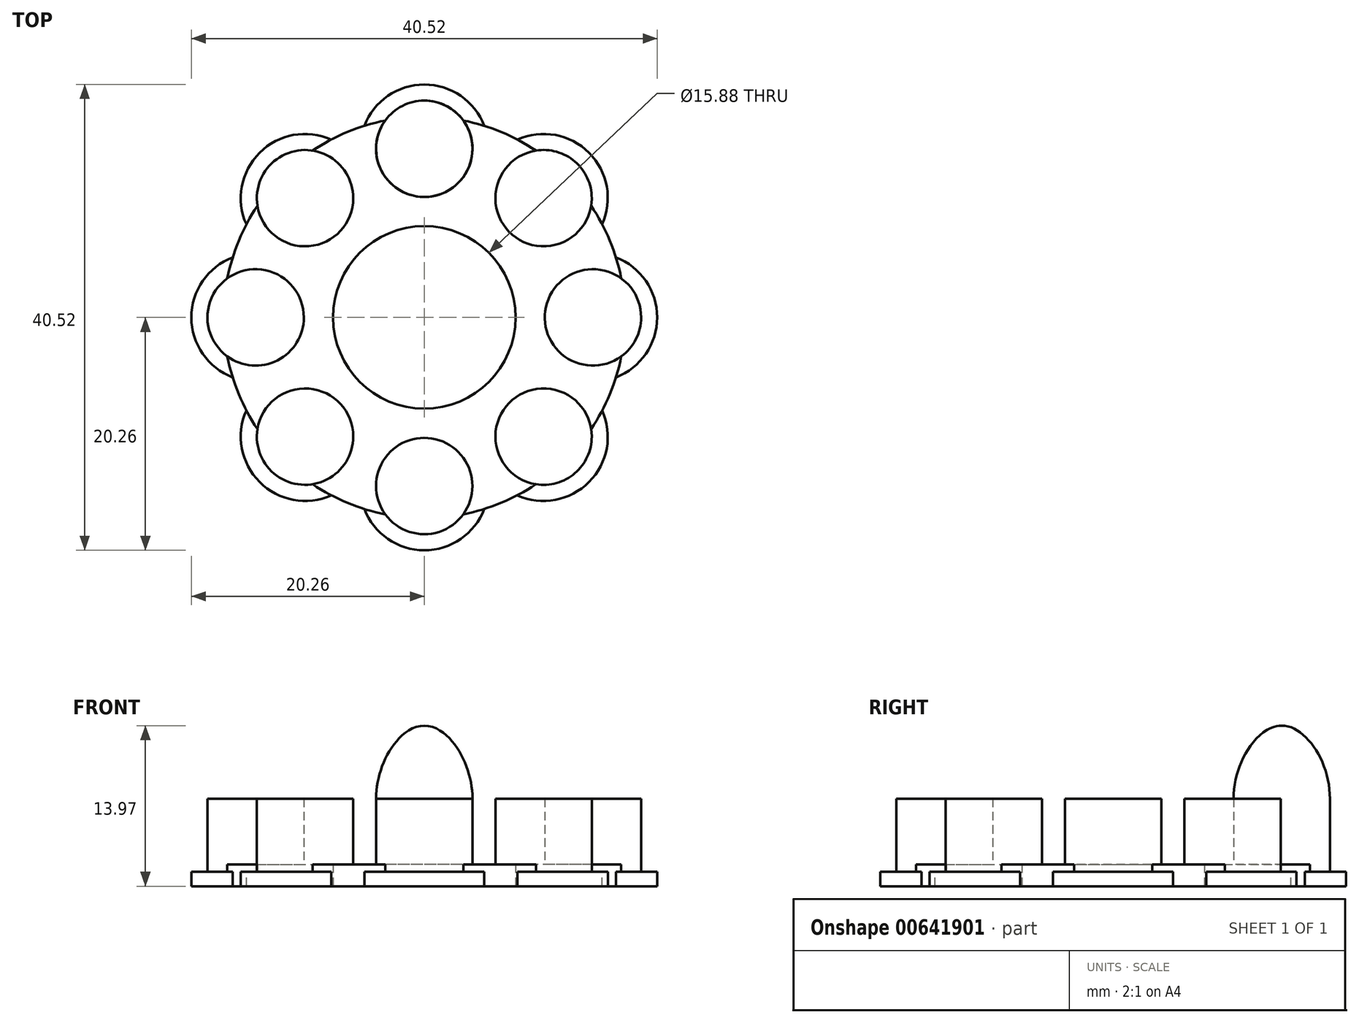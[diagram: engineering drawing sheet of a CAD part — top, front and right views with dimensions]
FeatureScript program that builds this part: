
annotation { "Feature Type Name" : "Feature", "Feature Type Description" : "" }
export const myFeature = defineFeature(function(context is Context, id is Id, definition is map)
    precondition{}
    {
        {
            var Q0;
            Q0=qCreatedBy(makeId("Top.planeOp"),FACE);
            var sketch = newSketch(context, id + "F0", { "sketchPlane" : qUnion([Q0])});
            skCircle(sketch, "E0", {"center": v(0, 14.67) * mm, "radius": 5.59 * mm});
            skCircle(sketch, "E1", {"center": v(0, 0) * mm, "radius": 7.94 * mm});
            skCircle(sketch, "E2", {"center": v(0, 14.67) * mm, "radius": 4.2 * mm});
            skCircle(sketch, "E3", {"center": v(0, 0) * mm, "radius": 17.46 * mm});
            skCircle(sketch, "E4.1.0", {"center": v(-10.37, 10.37) * mm, "radius": 4.2 * mm});
            skCircle(sketch, "E4.1.1", {"center": v(-10.37, 10.37) * mm, "radius": 5.59 * mm});
            skCircle(sketch, "E4.2.0", {"center": v(-14.67, 0) * mm, "radius": 4.2 * mm});
            skCircle(sketch, "E4.2.1", {"center": v(-14.67, 0) * mm, "radius": 5.59 * mm});
            skCircle(sketch, "E5.1.3.0", {"center": v(-10.37, -10.37) * mm, "radius": 4.2 * mm});
            skCircle(sketch, "E5.2.3.0", {"center": v(-10.37, -10.37) * mm, "radius": 5.59 * mm});
            skCircle(sketch, "E5.1.4.0", {"center": v(0, -14.67) * mm, "radius": 4.2 * mm});
            skCircle(sketch, "E5.2.4.0", {"center": v(0, -14.67) * mm, "radius": 5.59 * mm});
            skCircle(sketch, "E5.1.5.0", {"center": v(10.37, -10.37) * mm, "radius": 4.2 * mm});
            skCircle(sketch, "E5.2.5.0", {"center": v(10.37, -10.37) * mm, "radius": 5.59 * mm});
            skCircle(sketch, "E5.1.6.0", {"center": v(14.67, 0) * mm, "radius": 4.2 * mm});
            skCircle(sketch, "E5.2.6.0", {"center": v(14.67, 0) * mm, "radius": 5.59 * mm});
            skCircle(sketch, "E5.1.7.0", {"center": v(10.37, 10.37) * mm, "radius": 4.2 * mm});
            skCircle(sketch, "E5.2.7.0", {"center": v(10.37, 10.37) * mm, "radius": 5.59 * mm});
            skSolve(sketch);
        }
        {
            var Q0;
            {var subQ0=sQuery(id+"F0.wireOp",EDGE,"E3");var subQ1=sQuery(id+"F0.wireOp",EDGE,"E0");var subQ2=makeQuery(id+"F0.imprint","INTERSECT",VERTEX,{"disambiguationData":[OD(0.0)],"derivedFrom":[subQ1,subQ0]});Q0=makeQuery(id+"F0.imprint","IMPRINT",FACE,{"disambiguationData":[TD([[makeQuery(id+"F0.imprint","IMPRINT",EDGE,{"disambiguationData":[TD([[subQ2,1.0]])],"derivedFrom":subQ1}),1.0]])]});}
            var Q1;
            {var subQ0=sQuery(id+"F0.wireOp",EDGE,"E5.2.7.0");var subQ1=sQuery(id+"F0.wireOp",EDGE,"E3");var subQ2=makeQuery(id+"F0.imprint","INTERSECT",VERTEX,{"disambiguationData":[OD(0.0)],"derivedFrom":[subQ1,subQ0]});Q1=makeQuery(id+"F0.imprint","IMPRINT",FACE,{"disambiguationData":[TD([[makeQuery(id+"F0.imprint","IMPRINT",EDGE,{"disambiguationData":[TD([[subQ2,-1.0]])],"derivedFrom":subQ1}),1.0]])]});}
            var Q2;
            {var subQ0=sQuery(id+"F0.wireOp",EDGE,"E5.2.6.0");var subQ1=sQuery(id+"F0.wireOp",EDGE,"E3");var subQ2=makeQuery(id+"F0.imprint","INTERSECT",VERTEX,{"disambiguationData":[OD(0.0)],"derivedFrom":[subQ1,subQ0]});Q2=makeQuery(id+"F0.imprint","IMPRINT",FACE,{"disambiguationData":[TD([[makeQuery(id+"F0.imprint","IMPRINT",EDGE,{"disambiguationData":[TD([[subQ2,1.0]])],"derivedFrom":subQ1}),1.0]])]});}
            var Q3;
            {var subQ0=sQuery(id+"F0.wireOp",EDGE,"E5.2.5.0");var subQ1=sQuery(id+"F0.wireOp",EDGE,"E3");var subQ2=makeQuery(id+"F0.imprint","INTERSECT",VERTEX,{"disambiguationData":[OD(0.0)],"derivedFrom":[subQ1,subQ0]});Q3=makeQuery(id+"F0.imprint","IMPRINT",FACE,{"disambiguationData":[TD([[makeQuery(id+"F0.imprint","IMPRINT",EDGE,{"disambiguationData":[TD([[subQ2,-1.0]])],"derivedFrom":subQ1}),1.0]])]});}
            var Q4;
            {var subQ0=sQuery(id+"F0.wireOp",EDGE,"E5.2.4.0");var subQ1=sQuery(id+"F0.wireOp",EDGE,"E3");var subQ2=makeQuery(id+"F0.imprint","INTERSECT",VERTEX,{"disambiguationData":[OD(0.0)],"derivedFrom":[subQ1,subQ0]});Q4=makeQuery(id+"F0.imprint","IMPRINT",FACE,{"disambiguationData":[TD([[makeQuery(id+"F0.imprint","IMPRINT",EDGE,{"disambiguationData":[TD([[subQ2,-1.0]])],"derivedFrom":subQ1}),1.0]])]});}
            var Q5;
            {var subQ0=sQuery(id+"F0.wireOp",EDGE,"E5.2.3.0");var subQ1=sQuery(id+"F0.wireOp",EDGE,"E3");var subQ2=makeQuery(id+"F0.imprint","INTERSECT",VERTEX,{"disambiguationData":[OD(0.0)],"derivedFrom":[subQ1,subQ0]});Q5=makeQuery(id+"F0.imprint","IMPRINT",FACE,{"disambiguationData":[TD([[makeQuery(id+"F0.imprint","IMPRINT",EDGE,{"disambiguationData":[TD([[subQ2,-1.0]])],"derivedFrom":subQ1}),1.0]])]});}
            var Q6;
            {var subQ0=sQuery(id+"F0.wireOp",EDGE,"E4.2.1");var subQ1=sQuery(id+"F0.wireOp",EDGE,"E3");var subQ2=makeQuery(id+"F0.imprint","INTERSECT",VERTEX,{"disambiguationData":[OD(0.0)],"derivedFrom":[subQ1,subQ0]});Q6=makeQuery(id+"F0.imprint","IMPRINT",FACE,{"disambiguationData":[TD([[makeQuery(id+"F0.imprint","IMPRINT",EDGE,{"disambiguationData":[TD([[subQ2,-1.0]])],"derivedFrom":subQ1}),1.0]])]});}
            var Q7;
            {var subQ0=sQuery(id+"F0.wireOp",EDGE,"E4.1.1");var subQ1=sQuery(id+"F0.wireOp",EDGE,"E3");var subQ2=makeQuery(id+"F0.imprint","INTERSECT",VERTEX,{"disambiguationData":[OD(0.0)],"derivedFrom":[subQ1,subQ0]});Q7=makeQuery(id+"F0.imprint","IMPRINT",FACE,{"disambiguationData":[TD([[makeQuery(id+"F0.imprint","IMPRINT",EDGE,{"disambiguationData":[TD([[subQ2,-1.0]])],"derivedFrom":subQ1}),1.0]])]});}
            var Q8;
            Q8=makeQuery(id+"F0.imprint","IMPRINT",FACE,{"disambiguationData":[TD([[makeQuery(id+"F0.imprint","IMPRINT",EDGE,{"derivedFrom":sQuery(id+"F0.wireOp",EDGE,"E1")}),-1.0]])]});
            extrude(context, id + "F1", {"entities" : qUnion([Q0, Q1, Q2, Q3, Q4, Q5, Q6, Q7, Q8]), "depth" : 0.64 * mm, "offsetDistance" : 25.4 * mm});
        }
        {
            var Q0;
            Q0=qSketchRegion(id+"F0",true);
            var Q1;
            {var subQ0=sQuery(id+"F0.wireOp",EDGE,"E5.1.4.0");var subQ1=sQuery(id+"F0.wireOp",EDGE,"E3");var subQ2=makeQuery(id+"F0.imprint","INTERSECT",VERTEX,{"disambiguationData":[OD(0.0)],"derivedFrom":[subQ1,subQ0]});Q1=makeQuery(id+"F0.imprint","IMPRINT",FACE,{"disambiguationData":[TD([[makeQuery(id+"F0.imprint","IMPRINT",EDGE,{"disambiguationData":[TD([[subQ2,-1.0]])],"derivedFrom":subQ1}),-1.0]])]});}
            var Q2;
            {var subQ0=sQuery(id+"F0.wireOp",EDGE,"E5.1.4.0");var subQ1=sQuery(id+"F0.wireOp",EDGE,"E3");var subQ2=makeQuery(id+"F0.imprint","INTERSECT",VERTEX,{"disambiguationData":[OD(0.0)],"derivedFrom":[subQ1,subQ0]});Q2=makeQuery(id+"F0.imprint","IMPRINT",FACE,{"disambiguationData":[TD([[makeQuery(id+"F0.imprint","IMPRINT",EDGE,{"disambiguationData":[TD([[subQ2,-1.0]])],"derivedFrom":subQ1}),1.0]])]});}
            var Q3;
            {var subQ0=sQuery(id+"F0.wireOp",EDGE,"E5.1.5.0");var subQ1=sQuery(id+"F0.wireOp",EDGE,"E3");var subQ2=makeQuery(id+"F0.imprint","INTERSECT",VERTEX,{"disambiguationData":[OD(0.0)],"derivedFrom":[subQ1,subQ0]});Q3=makeQuery(id+"F0.imprint","IMPRINT",FACE,{"disambiguationData":[TD([[makeQuery(id+"F0.imprint","IMPRINT",EDGE,{"disambiguationData":[TD([[subQ2,-1.0]])],"derivedFrom":subQ1}),1.0]])]});}
            var Q4;
            {var subQ0=sQuery(id+"F0.wireOp",EDGE,"E5.1.5.0");var subQ1=sQuery(id+"F0.wireOp",EDGE,"E3");var subQ2=makeQuery(id+"F0.imprint","INTERSECT",VERTEX,{"disambiguationData":[OD(0.0)],"derivedFrom":[subQ1,subQ0]});Q4=makeQuery(id+"F0.imprint","IMPRINT",FACE,{"disambiguationData":[TD([[makeQuery(id+"F0.imprint","IMPRINT",EDGE,{"disambiguationData":[TD([[subQ2,-1.0]])],"derivedFrom":subQ1}),-1.0]])]});}
            var Q5;
            {var subQ0=sQuery(id+"F0.wireOp",EDGE,"E5.1.6.0");var subQ1=sQuery(id+"F0.wireOp",EDGE,"E3");var subQ2=makeQuery(id+"F0.imprint","INTERSECT",VERTEX,{"disambiguationData":[OD(0.0)],"derivedFrom":[subQ1,subQ0]});Q5=makeQuery(id+"F0.imprint","IMPRINT",FACE,{"disambiguationData":[TD([[makeQuery(id+"F0.imprint","IMPRINT",EDGE,{"disambiguationData":[TD([[subQ2,1.0]])],"derivedFrom":subQ1}),-1.0]])]});}
            var Q6;
            {var subQ0=sQuery(id+"F0.wireOp",EDGE,"E5.1.6.0");var subQ1=sQuery(id+"F0.wireOp",EDGE,"E3");var subQ2=makeQuery(id+"F0.imprint","INTERSECT",VERTEX,{"disambiguationData":[OD(0.0)],"derivedFrom":[subQ1,subQ0]});Q6=makeQuery(id+"F0.imprint","IMPRINT",FACE,{"disambiguationData":[TD([[makeQuery(id+"F0.imprint","IMPRINT",EDGE,{"disambiguationData":[TD([[subQ2,1.0]])],"derivedFrom":subQ1}),1.0]])]});}
            var Q7;
            {var subQ0=sQuery(id+"F0.wireOp",EDGE,"E5.1.7.0");var subQ1=sQuery(id+"F0.wireOp",EDGE,"E3");var subQ2=makeQuery(id+"F0.imprint","INTERSECT",VERTEX,{"disambiguationData":[OD(0.0)],"derivedFrom":[subQ1,subQ0]});Q7=makeQuery(id+"F0.imprint","IMPRINT",FACE,{"disambiguationData":[TD([[makeQuery(id+"F0.imprint","IMPRINT",EDGE,{"disambiguationData":[TD([[subQ2,-1.0]])],"derivedFrom":subQ1}),1.0]])]});}
            var Q8;
            {var subQ0=sQuery(id+"F0.wireOp",EDGE,"E5.1.7.0");var subQ1=sQuery(id+"F0.wireOp",EDGE,"E3");var subQ2=makeQuery(id+"F0.imprint","INTERSECT",VERTEX,{"disambiguationData":[OD(0.0)],"derivedFrom":[subQ1,subQ0]});Q8=makeQuery(id+"F0.imprint","IMPRINT",FACE,{"disambiguationData":[TD([[makeQuery(id+"F0.imprint","IMPRINT",EDGE,{"disambiguationData":[TD([[subQ2,-1.0]])],"derivedFrom":subQ1}),-1.0]])]});}
            var Q9;
            {var subQ0=sQuery(id+"F0.wireOp",EDGE,"E4.1.0");var subQ1=sQuery(id+"F0.wireOp",EDGE,"E3");var subQ2=makeQuery(id+"F0.imprint","INTERSECT",VERTEX,{"disambiguationData":[OD(0.0)],"derivedFrom":[subQ1,subQ0]});Q9=makeQuery(id+"F0.imprint","IMPRINT",FACE,{"disambiguationData":[TD([[makeQuery(id+"F0.imprint","IMPRINT",EDGE,{"disambiguationData":[TD([[subQ2,-1.0]])],"derivedFrom":subQ1}),1.0]])]});}
            var Q10;
            {var subQ0=sQuery(id+"F0.wireOp",EDGE,"E4.1.0");var subQ1=sQuery(id+"F0.wireOp",EDGE,"E3");var subQ2=makeQuery(id+"F0.imprint","INTERSECT",VERTEX,{"disambiguationData":[OD(0.0)],"derivedFrom":[subQ1,subQ0]});Q10=makeQuery(id+"F0.imprint","IMPRINT",FACE,{"disambiguationData":[TD([[makeQuery(id+"F0.imprint","IMPRINT",EDGE,{"disambiguationData":[TD([[subQ2,-1.0]])],"derivedFrom":subQ1}),-1.0]])]});}
            var Q11;
            {var subQ0=sQuery(id+"F0.wireOp",EDGE,"E4.2.0");var subQ1=sQuery(id+"F0.wireOp",EDGE,"E3");var subQ2=makeQuery(id+"F0.imprint","INTERSECT",VERTEX,{"disambiguationData":[OD(0.0)],"derivedFrom":[subQ1,subQ0]});Q11=makeQuery(id+"F0.imprint","IMPRINT",FACE,{"disambiguationData":[TD([[makeQuery(id+"F0.imprint","IMPRINT",EDGE,{"disambiguationData":[TD([[subQ2,-1.0]])],"derivedFrom":subQ1}),1.0]])]});}
            var Q12;
            {var subQ0=sQuery(id+"F0.wireOp",EDGE,"E3");var subQ1=sQuery(id+"F0.wireOp",EDGE,"E2");var subQ2=makeQuery(id+"F0.imprint","INTERSECT",VERTEX,{"disambiguationData":[OD(0.0)],"derivedFrom":[subQ1,subQ0]});Q12=makeQuery(id+"F0.imprint","IMPRINT",FACE,{"disambiguationData":[TD([[makeQuery(id+"F0.imprint","IMPRINT",EDGE,{"disambiguationData":[TD([[subQ2,1.0]])],"derivedFrom":subQ1}),1.0]])]});}
            var Q13;
            {var subQ0=sQuery(id+"F0.wireOp",EDGE,"E3");var subQ1=sQuery(id+"F0.wireOp",EDGE,"E2");var subQ2=makeQuery(id+"F0.imprint","INTERSECT",VERTEX,{"disambiguationData":[OD(0.0)],"derivedFrom":[subQ1,subQ0]});Q13=makeQuery(id+"F0.imprint","IMPRINT",FACE,{"disambiguationData":[TD([[makeQuery(id+"F0.imprint","IMPRINT",EDGE,{"disambiguationData":[TD([[subQ2,-1.0]])],"derivedFrom":subQ1}),1.0]])]});}
            var Q14;
            {var subQ0=sQuery(id+"F0.wireOp",EDGE,"E5.1.3.0");var subQ1=sQuery(id+"F0.wireOp",EDGE,"E3");var subQ2=makeQuery(id+"F0.imprint","INTERSECT",VERTEX,{"disambiguationData":[OD(0.0)],"derivedFrom":[subQ1,subQ0]});Q14=makeQuery(id+"F0.imprint","IMPRINT",FACE,{"disambiguationData":[TD([[makeQuery(id+"F0.imprint","IMPRINT",EDGE,{"disambiguationData":[TD([[subQ2,-1.0]])],"derivedFrom":subQ1}),-1.0]])]});}
            var Q15;
            {var subQ0=sQuery(id+"F0.wireOp",EDGE,"E5.1.3.0");var subQ1=sQuery(id+"F0.wireOp",EDGE,"E3");var subQ2=makeQuery(id+"F0.imprint","INTERSECT",VERTEX,{"disambiguationData":[OD(0.0)],"derivedFrom":[subQ1,subQ0]});Q15=makeQuery(id+"F0.imprint","IMPRINT",FACE,{"disambiguationData":[TD([[makeQuery(id+"F0.imprint","IMPRINT",EDGE,{"disambiguationData":[TD([[subQ2,-1.0]])],"derivedFrom":subQ1}),1.0]])]});}
            var Q16;
            {var subQ0=sQuery(id+"F0.wireOp",EDGE,"E4.2.0");var subQ1=sQuery(id+"F0.wireOp",EDGE,"E3");var subQ2=makeQuery(id+"F0.imprint","INTERSECT",VERTEX,{"disambiguationData":[OD(0.0)],"derivedFrom":[subQ1,subQ0]});Q16=makeQuery(id+"F0.imprint","IMPRINT",FACE,{"disambiguationData":[TD([[makeQuery(id+"F0.imprint","IMPRINT",EDGE,{"disambiguationData":[TD([[subQ2,-1.0]])],"derivedFrom":subQ1}),-1.0]])]});}
            extrude(context, id + "F2", {"entities" : qUnion([Q0, Q1, Q2, Q3, Q4, Q5, Q6, Q7, Q8, Q9, Q10, Q11, Q12, Q13, Q14, Q15, Q16]), "operationType" : NewBodyOperationType.ADD, "oppositeDirection" : true, "depth" : 1.27 * mm, "offsetDistance" : 25.4 * mm});
        }
        {
            var Q0;
            {var subQ0=sQuery(id+"F0.wireOp",EDGE,"E5.1.5.0");var subQ1=sQuery(id+"F0.wireOp",EDGE,"E3");var subQ2=makeQuery(id+"F0.imprint","INTERSECT",VERTEX,{"disambiguationData":[OD(0.0)],"derivedFrom":[subQ1,subQ0]});Q0=makeQuery(id+"F0.imprint","IMPRINT",FACE,{"disambiguationData":[TD([[makeQuery(id+"F0.imprint","IMPRINT",EDGE,{"disambiguationData":[TD([[subQ2,-1.0]])],"derivedFrom":subQ1}),1.0]])]});}
            var Q1;
            {var subQ0=sQuery(id+"F0.wireOp",EDGE,"E5.1.5.0");var subQ1=sQuery(id+"F0.wireOp",EDGE,"E3");var subQ2=makeQuery(id+"F0.imprint","INTERSECT",VERTEX,{"disambiguationData":[OD(0.0)],"derivedFrom":[subQ1,subQ0]});Q1=makeQuery(id+"F0.imprint","IMPRINT",FACE,{"disambiguationData":[TD([[makeQuery(id+"F0.imprint","IMPRINT",EDGE,{"disambiguationData":[TD([[subQ2,-1.0]])],"derivedFrom":subQ1}),-1.0]])]});}
            var Q2;
            {var subQ0=sQuery(id+"F0.wireOp",EDGE,"E5.1.4.0");var subQ1=sQuery(id+"F0.wireOp",EDGE,"E3");var subQ2=makeQuery(id+"F0.imprint","INTERSECT",VERTEX,{"disambiguationData":[OD(0.0)],"derivedFrom":[subQ1,subQ0]});Q2=makeQuery(id+"F0.imprint","IMPRINT",FACE,{"disambiguationData":[TD([[makeQuery(id+"F0.imprint","IMPRINT",EDGE,{"disambiguationData":[TD([[subQ2,-1.0]])],"derivedFrom":subQ1}),-1.0]])]});}
            var Q3;
            {var subQ0=sQuery(id+"F0.wireOp",EDGE,"E5.1.4.0");var subQ1=sQuery(id+"F0.wireOp",EDGE,"E3");var subQ2=makeQuery(id+"F0.imprint","INTERSECT",VERTEX,{"disambiguationData":[OD(0.0)],"derivedFrom":[subQ1,subQ0]});Q3=makeQuery(id+"F0.imprint","IMPRINT",FACE,{"disambiguationData":[TD([[makeQuery(id+"F0.imprint","IMPRINT",EDGE,{"disambiguationData":[TD([[subQ2,-1.0]])],"derivedFrom":subQ1}),1.0]])]});}
            var Q4;
            {var subQ0=sQuery(id+"F0.wireOp",EDGE,"E5.1.3.0");var subQ1=sQuery(id+"F0.wireOp",EDGE,"E3");var subQ2=makeQuery(id+"F0.imprint","INTERSECT",VERTEX,{"disambiguationData":[OD(0.0)],"derivedFrom":[subQ1,subQ0]});Q4=makeQuery(id+"F0.imprint","IMPRINT",FACE,{"disambiguationData":[TD([[makeQuery(id+"F0.imprint","IMPRINT",EDGE,{"disambiguationData":[TD([[subQ2,-1.0]])],"derivedFrom":subQ1}),1.0]])]});}
            var Q5;
            {var subQ0=sQuery(id+"F0.wireOp",EDGE,"E5.1.3.0");var subQ1=sQuery(id+"F0.wireOp",EDGE,"E3");var subQ2=makeQuery(id+"F0.imprint","INTERSECT",VERTEX,{"disambiguationData":[OD(0.0)],"derivedFrom":[subQ1,subQ0]});Q5=makeQuery(id+"F0.imprint","IMPRINT",FACE,{"disambiguationData":[TD([[makeQuery(id+"F0.imprint","IMPRINT",EDGE,{"disambiguationData":[TD([[subQ2,-1.0]])],"derivedFrom":subQ1}),-1.0]])]});}
            var Q6;
            {var subQ0=sQuery(id+"F0.wireOp",EDGE,"E4.2.0");var subQ1=sQuery(id+"F0.wireOp",EDGE,"E3");var subQ2=makeQuery(id+"F0.imprint","INTERSECT",VERTEX,{"disambiguationData":[OD(0.0)],"derivedFrom":[subQ1,subQ0]});Q6=makeQuery(id+"F0.imprint","IMPRINT",FACE,{"disambiguationData":[TD([[makeQuery(id+"F0.imprint","IMPRINT",EDGE,{"disambiguationData":[TD([[subQ2,-1.0]])],"derivedFrom":subQ1}),1.0]])]});}
            var Q7;
            {var subQ0=sQuery(id+"F0.wireOp",EDGE,"E4.2.0");var subQ1=sQuery(id+"F0.wireOp",EDGE,"E3");var subQ2=makeQuery(id+"F0.imprint","INTERSECT",VERTEX,{"disambiguationData":[OD(0.0)],"derivedFrom":[subQ1,subQ0]});Q7=makeQuery(id+"F0.imprint","IMPRINT",FACE,{"disambiguationData":[TD([[makeQuery(id+"F0.imprint","IMPRINT",EDGE,{"disambiguationData":[TD([[subQ2,-1.0]])],"derivedFrom":subQ1}),-1.0]])]});}
            var Q8;
            {var subQ0=sQuery(id+"F0.wireOp",EDGE,"E4.1.0");var subQ1=sQuery(id+"F0.wireOp",EDGE,"E3");var subQ2=makeQuery(id+"F0.imprint","INTERSECT",VERTEX,{"disambiguationData":[OD(0.0)],"derivedFrom":[subQ1,subQ0]});Q8=makeQuery(id+"F0.imprint","IMPRINT",FACE,{"disambiguationData":[TD([[makeQuery(id+"F0.imprint","IMPRINT",EDGE,{"disambiguationData":[TD([[subQ2,-1.0]])],"derivedFrom":subQ1}),1.0]])]});}
            var Q9;
            {var subQ0=sQuery(id+"F0.wireOp",EDGE,"E4.1.0");var subQ1=sQuery(id+"F0.wireOp",EDGE,"E3");var subQ2=makeQuery(id+"F0.imprint","INTERSECT",VERTEX,{"disambiguationData":[OD(0.0)],"derivedFrom":[subQ1,subQ0]});Q9=makeQuery(id+"F0.imprint","IMPRINT",FACE,{"disambiguationData":[TD([[makeQuery(id+"F0.imprint","IMPRINT",EDGE,{"disambiguationData":[TD([[subQ2,-1.0]])],"derivedFrom":subQ1}),-1.0]])]});}
            var Q10;
            {var subQ0=sQuery(id+"F0.wireOp",EDGE,"E3");var subQ1=sQuery(id+"F0.wireOp",EDGE,"E2");var subQ2=makeQuery(id+"F0.imprint","INTERSECT",VERTEX,{"disambiguationData":[OD(0.0)],"derivedFrom":[subQ1,subQ0]});Q10=makeQuery(id+"F0.imprint","IMPRINT",FACE,{"disambiguationData":[TD([[makeQuery(id+"F0.imprint","IMPRINT",EDGE,{"disambiguationData":[TD([[subQ2,1.0]])],"derivedFrom":subQ1}),1.0]])]});}
            var Q11;
            {var subQ0=sQuery(id+"F0.wireOp",EDGE,"E3");var subQ1=sQuery(id+"F0.wireOp",EDGE,"E2");var subQ2=makeQuery(id+"F0.imprint","INTERSECT",VERTEX,{"disambiguationData":[OD(0.0)],"derivedFrom":[subQ1,subQ0]});Q11=makeQuery(id+"F0.imprint","IMPRINT",FACE,{"disambiguationData":[TD([[makeQuery(id+"F0.imprint","IMPRINT",EDGE,{"disambiguationData":[TD([[subQ2,-1.0]])],"derivedFrom":subQ1}),1.0]])]});}
            var Q12;
            {var subQ0=sQuery(id+"F0.wireOp",EDGE,"E5.1.7.0");var subQ1=sQuery(id+"F0.wireOp",EDGE,"E3");var subQ2=makeQuery(id+"F0.imprint","INTERSECT",VERTEX,{"disambiguationData":[OD(0.0)],"derivedFrom":[subQ1,subQ0]});Q12=makeQuery(id+"F0.imprint","IMPRINT",FACE,{"disambiguationData":[TD([[makeQuery(id+"F0.imprint","IMPRINT",EDGE,{"disambiguationData":[TD([[subQ2,-1.0]])],"derivedFrom":subQ1}),1.0]])]});}
            var Q13;
            {var subQ0=sQuery(id+"F0.wireOp",EDGE,"E5.1.7.0");var subQ1=sQuery(id+"F0.wireOp",EDGE,"E3");var subQ2=makeQuery(id+"F0.imprint","INTERSECT",VERTEX,{"disambiguationData":[OD(0.0)],"derivedFrom":[subQ1,subQ0]});Q13=makeQuery(id+"F0.imprint","IMPRINT",FACE,{"disambiguationData":[TD([[makeQuery(id+"F0.imprint","IMPRINT",EDGE,{"disambiguationData":[TD([[subQ2,-1.0]])],"derivedFrom":subQ1}),-1.0]])]});}
            var Q14;
            {var subQ0=sQuery(id+"F0.wireOp",EDGE,"E5.1.6.0");var subQ1=sQuery(id+"F0.wireOp",EDGE,"E3");var subQ2=makeQuery(id+"F0.imprint","INTERSECT",VERTEX,{"disambiguationData":[OD(0.0)],"derivedFrom":[subQ1,subQ0]});Q14=makeQuery(id+"F0.imprint","IMPRINT",FACE,{"disambiguationData":[TD([[makeQuery(id+"F0.imprint","IMPRINT",EDGE,{"disambiguationData":[TD([[subQ2,1.0]])],"derivedFrom":subQ1}),1.0]])]});}
            var Q15;
            {var subQ0=sQuery(id+"F0.wireOp",EDGE,"E5.1.6.0");var subQ1=sQuery(id+"F0.wireOp",EDGE,"E3");var subQ2=makeQuery(id+"F0.imprint","INTERSECT",VERTEX,{"disambiguationData":[OD(0.0)],"derivedFrom":[subQ1,subQ0]});Q15=makeQuery(id+"F0.imprint","IMPRINT",FACE,{"disambiguationData":[TD([[makeQuery(id+"F0.imprint","IMPRINT",EDGE,{"disambiguationData":[TD([[subQ2,1.0]])],"derivedFrom":subQ1}),-1.0]])]});}
            extrude(context, id + "F3", {"entities" : qUnion([Q0, Q1, Q2, Q3, Q4, Q5, Q6, Q7, Q8, Q9, Q10, Q11, Q12, Q13, Q14, Q15]), "operationType" : NewBodyOperationType.ADD, "depth" : 6.35 * mm, "offsetDistance" : 25.4 * mm});
        }
        {
            var Q0;
            Q0=qCreatedBy(makeId("Right.planeOp"),FACE);
            var sketch = newSketch(context, id + "F4", { "sketchPlane" : qUnion([Q0])});
            skLineSegment(sketch, "E6", {"start": v(14.67, 6.35) * mm, "end": v(14.67, 12.7) * mm});
            skFitSpline(sketch, "E7", {"points": [v(14.67, 12.7) * mm, v(18.86, 6.35) * mm], "startDerivative": vector(6.29, 0) * mm, "endDerivative": vector(0, -9.53) * mm});
            skLineSegment(sketch, "E8", {"start": v(18.86, 6.35) * mm, "end": v(14.67, 6.35) * mm});
            skLineSegment(sketch, "E9", {"start": v(0, 0) * mm, "end": v(0, 29.34) * mm, "construction": true});
            skPoint(sketch, "E10", {"position": v(14.67, 9.53) * mm});
            skLineSegment(sketch, "E11", {"start": v(25.4, -1.27) * mm, "end": v(25.4, 12.7) * mm, "construction": true});
            skPoint(sketch, "E12", {"position": v(16.76, 6.35) * mm});
            skSolve(sketch);
        }
        {
            var Q0;
            Q0=makeQuery(id+"F4.imprint","IMPRINT",FACE,{"disambiguationData":[TD([[makeQuery(id+"F4.imprint","IMPRINT",EDGE,{"derivedFrom":sQuery(id+"F4.wireOp",EDGE,"E6")}),-1.0]])]});
            var Q1;
            Q1=sQuery(id+"F4.wireOp",EDGE,"E6");
            revolve(context, id + "F5", {"operationType" : NewBodyOperationType.ADD, "entities" : qUnion([Q0]), "axis" : qUnion([Q1]), "revolveType" : RevolveType.FULL});
        }
    });
